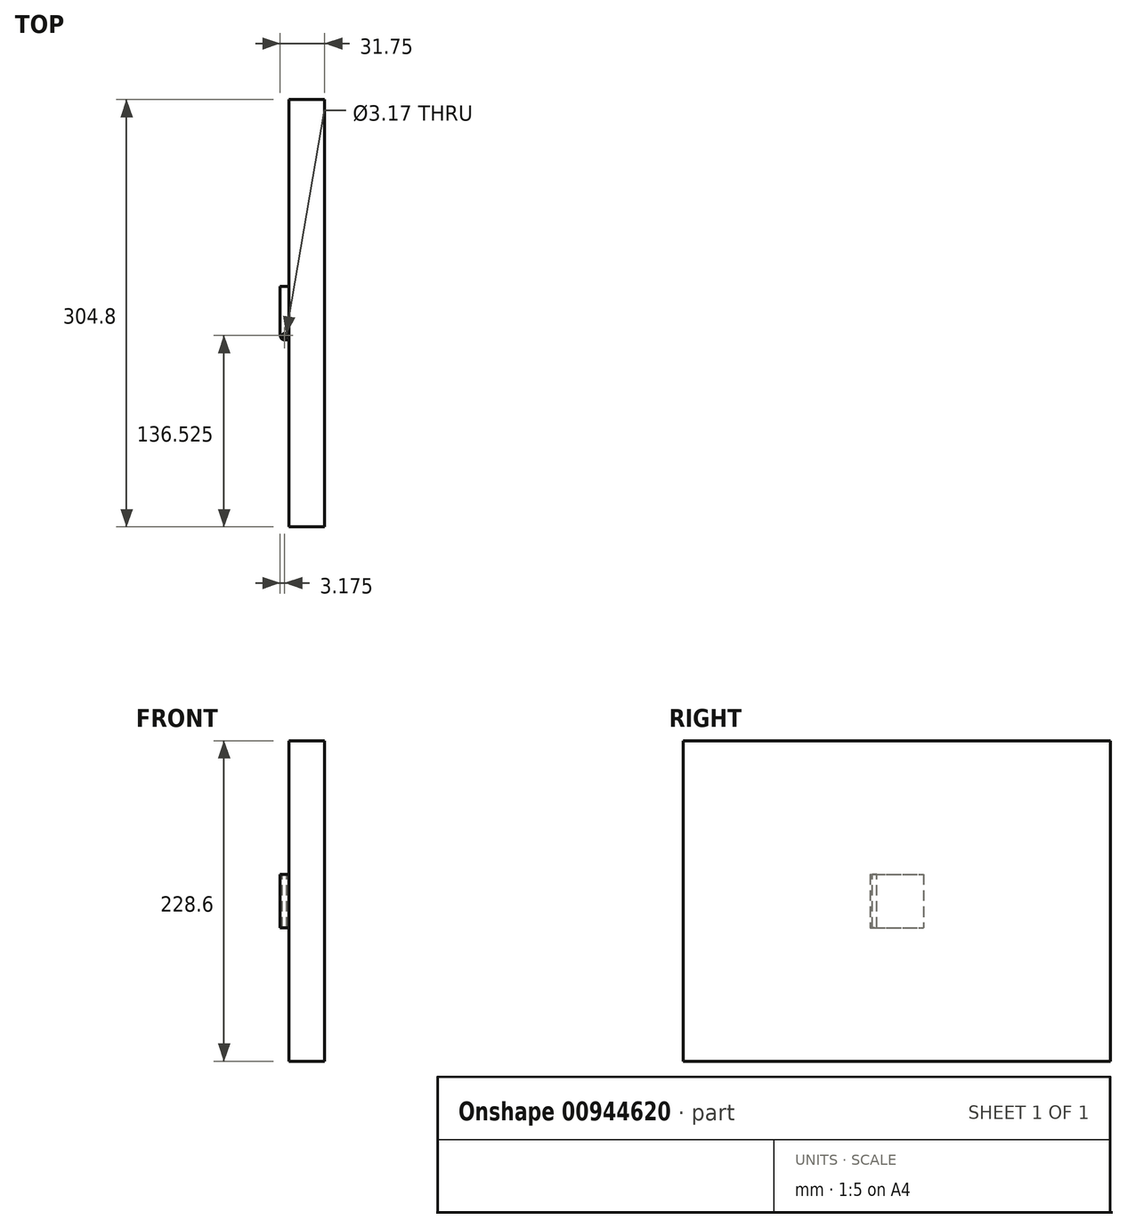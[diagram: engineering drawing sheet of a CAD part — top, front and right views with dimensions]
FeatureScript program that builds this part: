
annotation { "Feature Type Name" : "Feature", "Feature Type Description" : "" }
export const myFeature = defineFeature(function(context is Context, id is Id, definition is map)
    precondition{}
    {
        {
            var Q0;
            Q0=qCreatedBy(makeId("Right.planeOp"),FACE);
            var sketch = newSketch(context, id + "F0", { "sketchPlane" : qUnion([Q0])});
            skLineSegment(sketch, "E0.bottom", {"start": v(152.4, 114.3) * mm, "end": v(-152.4, 114.3) * mm});
            skLineSegment(sketch, "E0.top", {"start": v(152.4, -114.3) * mm, "end": v(-152.4, -114.3) * mm});
            skLineSegment(sketch, "E0.left", {"start": v(152.4, 114.3) * mm, "end": v(152.4, -114.3) * mm});
            skLineSegment(sketch, "E0.right", {"start": v(-152.4, 114.3) * mm, "end": v(-152.4, -114.3) * mm});
            skPoint(sketch, "E0.middle", {"position": v(0, 0) * mm});
            skSolve(sketch);
        }
        {
            var Q0;
            Q0=makeQuery(id+"F0.imprint","IMPRINT",FACE,{"disambiguationData":[TD([[makeQuery(id+"F0.imprint","IMPRINT",EDGE,{"derivedFrom":sQuery(id+"F0.wireOp",EDGE,"E0.bottom")}),1.0]])]});
            extrude(context, id + "F1", {"entities" : qUnion([Q0]), "depth" : 25.4 * mm, "offsetDistance" : 25.4 * mm});
        }
        {
            var Q0;
            Q0=qCreatedBy(makeId("Front.planeOp"),FACE);
            var sketch = newSketch(context, id + "F2", { "sketchPlane" : qUnion([Q0])});
            skLineSegment(sketch, "E1.bottom", {"start": v(0, 19.05) * mm, "end": v(-3.17, 19.05) * mm});
            skLineSegment(sketch, "E1.top", {"start": v(0, -19.05) * mm, "end": v(-3.18, -19.05) * mm});
            skPoint(sketch, "E1.middle", {"position": v(0, 0) * mm});
            skLineSegment(sketch, "E2.bottom", {"start": v(0, 19.05) * mm, "end": v(-6.35, 19.05) * mm});
            skLineSegment(sketch, "E2.top", {"start": v(0, -19.05) * mm, "end": v(-6.35, -19.05) * mm});
            skLineSegment(sketch, "E2.left", {"start": v(0, 19.05) * mm, "end": v(0, -19.05) * mm});
            skLineSegment(sketch, "E2.right", {"start": v(-6.35, 19.05) * mm, "end": v(-6.35, -19.05) * mm});
            skPoint(sketch, "E2.middle", {"position": v(-3.18, 0) * mm});
            skPoint(sketch, "E3.orphan", {"position": v(3.18, 19.05) * mm});
            skPoint(sketch, "E4.orphan", {"position": v(3.17, -19.05) * mm});
            skSolve(sketch);
        }
        {
            var Q0;
            {var subQ0=sQuery(id+"F2.wireOp",EDGE,"E2.left");Q0=makeQuery(id+"F2.imprint","IMPRINT",FACE,{"disambiguationData":[TD([[makeQuery(id+"F2.imprint","IMPRINT",EDGE,{"derivedFrom":subQ0}),-1.0]])]});}
            extrude(context, id + "F3", {"entities" : qUnion([Q0]), "operationType" : NewBodyOperationType.ADD, "endBound" : BoundingType.SYMMETRIC, "depth" : 38.1 * mm, "offsetDistance" : 25.4 * mm});
        }
        {
            var Q0;
            Q0=makeQuery(id+"F3.opExtrude","SWEPT_FACE",FACE,{"disambiguationData":[OSD([sQuery(id+"F2.wireOp",EDGE,"E2.bottom")])]});
            var sketch = newSketch(context, id + "F4", { "sketchPlane" : qUnion([Q0])});
            skCircle(sketch, "E5", {"center": v(-3.18, -15.88) * mm, "radius": 1.59 * mm});
            skPoint(sketch, "E5.centerSnap0", {"position": v(-3.18, -19.05) * mm});
            skSolve(sketch);
        }
        {
            var Q0;
            Q0=sQuery(id+"F4.wireOp",VERTEX,"E5.center");
            var Q1;
            Q1=makeQuery(id+"F1.opExtrude","SWEPT_BODY",BODY,{"disambiguationData":[OSD([sQuery(id+"F0.wireOp",EDGE,"E0.bottom"),sQuery(id+"F0.wireOp",EDGE,"E0.top"),sQuery(id+"F0.wireOp",EDGE,"E0.left"),sQuery(id+"F0.wireOp",EDGE,"E0.right")])]});
            hole(context, id + "F5", {"style" : HoleStyle.SIMPLE, "endStyle" : HoleEndStyle.THROUGH, "holeDiameter" : 3.17 * mm, "majorDiameter" : 6.35 * mm, "isTappedThrough" : true, "tappedDepth" : 12.7 * mm, "tapClearance" : 3, "locations" : qUnion([Q0]), "scope" : qUnion([Q1])});
        }
        {
            var Q0;
            Q0=makeQuery(id+"F3.opExtrude","CAP_EDGE",EDGE,{"disambiguationData":[OSD([sQuery(id+"F2.wireOp",EDGE,"E2.right")])],"isStart":false});
            fillet(context, id + "F6", {"entities" : qUnion([Q0]), "radius" : 3.17 * mm, "tangentPropagation" : true, "allowEdgeOverflow" : false});
        }
    });
